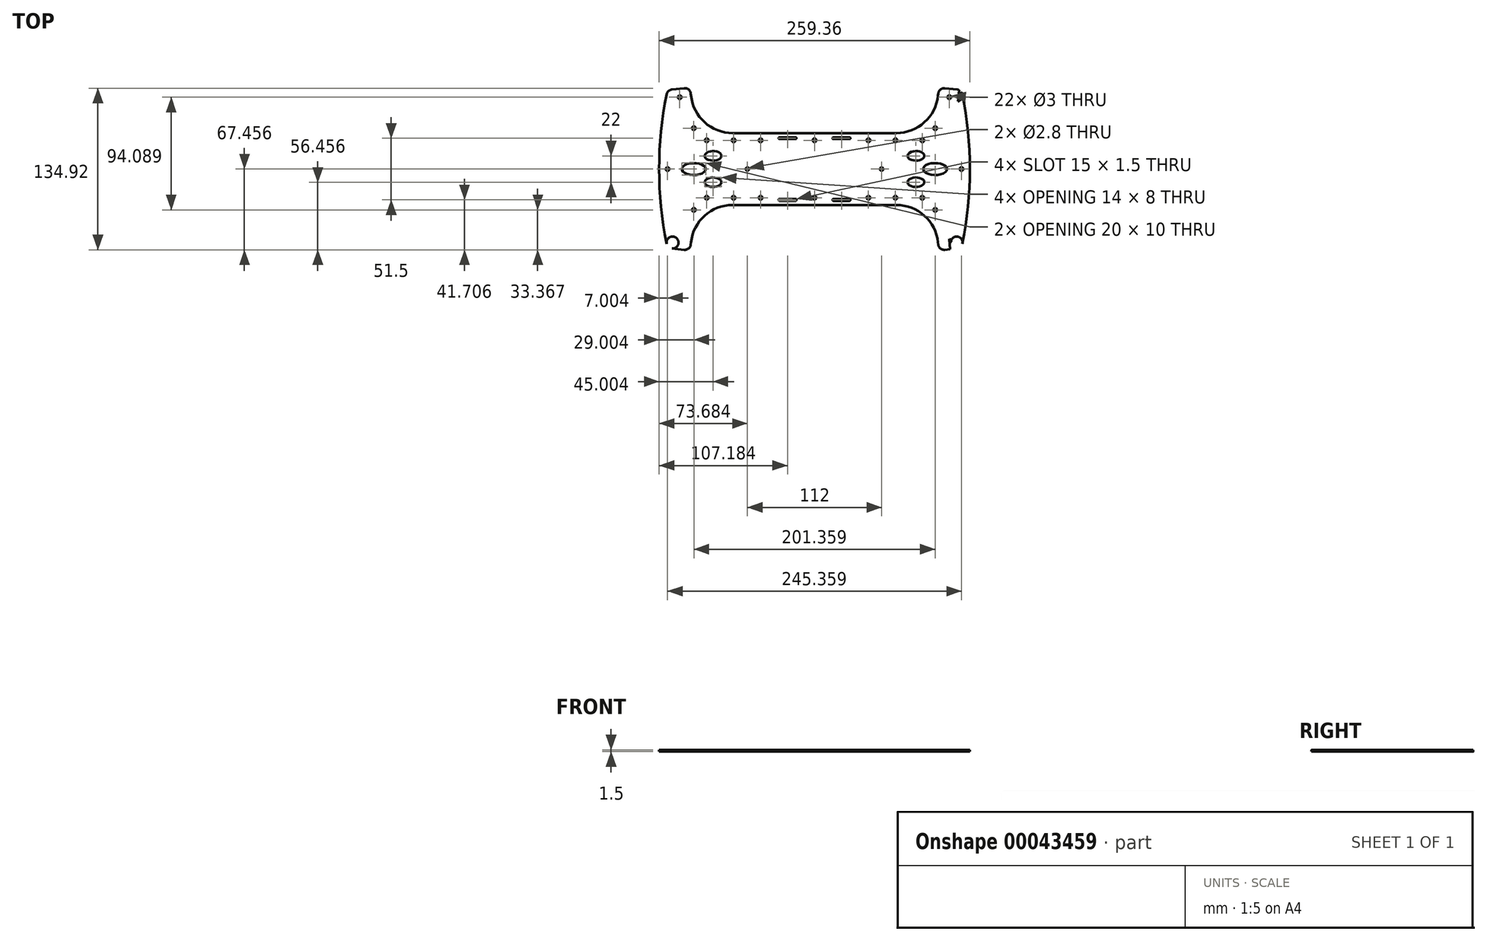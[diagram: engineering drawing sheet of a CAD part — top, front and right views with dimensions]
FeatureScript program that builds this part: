
annotation { "Feature Type Name" : "Feature", "Feature Type Description" : "" }
export const myFeature = defineFeature(function(context is Context, id is Id, definition is map)
    precondition{}
    {
        {
            var Q0;
            Q0=qCreatedBy(makeId("Top.planeOp"),FACE);
            var sketch = newSketch(context, id + "F0", { "sketchPlane" : qUnion([Q0])});
            skLineSegment(sketch, "E0", {"start": v(-133.26, 711.65) * mm, "end": v(112.1, 711.65) * mm});
            skCircle(sketch, "E1", {"center": v(-123.08, 771.65) * mm, "radius": 1.5 * mm});
            skCircle(sketch, "E2", {"center": v(-111.3, 745.73) * mm, "radius": 1.5 * mm});
            skCircle(sketch, "E3", {"center": v(90.15, 745.73) * mm, "radius": 1.5 * mm});
            skCircle(sketch, "E4", {"center": v(101.92, 771.65) * mm, "radius": 1.5 * mm});
            skLineSegment(sketch, "E5", {"start": v(-126.98, 737.05) * mm, "end": v(-131.27, 777.82) * mm});
            skLineSegment(sketch, "E6", {"start": v(-131.27, 777.82) * mm, "end": v(-116.35, 779.4) * mm});
            skLineSegment(sketch, "E7", {"start": v(-116.35, 779.4) * mm, "end": v(-112.06, 738.62) * mm});
            skLineSegment(sketch, "E8", {"start": v(-112.06, 738.62) * mm, "end": v(-126.98, 737.05) * mm});
            skLineSegment(sketch, "E9", {"start": v(-133.26, 777.61) * mm, "end": v(-119.33, 779.08) * mm});
            skLineSegment(sketch, "E10", {"start": v(-133.26, 777.61) * mm, "end": v(-133.26, 711.65) * mm});
            skLineSegment(sketch, "E11", {"start": v(95.2, 779.4) * mm, "end": v(110.11, 777.82) * mm});
            skLineSegment(sketch, "E12", {"start": v(110.11, 777.82) * mm, "end": v(105.83, 737.05) * mm});
            skLineSegment(sketch, "E13", {"start": v(105.83, 737.05) * mm, "end": v(90.91, 738.62) * mm});
            skLineSegment(sketch, "E14", {"start": v(90.91, 738.62) * mm, "end": v(95.2, 779.4) * mm});
            skLineSegment(sketch, "E15", {"start": v(98.18, 779.08) * mm, "end": v(112.1, 777.61) * mm});
            skLineSegment(sketch, "E16", {"start": v(112.1, 777.61) * mm, "end": v(112.1, 711.65) * mm});
            skLineSegment(sketch, "E17", {"start": v(-78.86, 741.65) * mm, "end": v(57.7, 741.65) * mm});
            skLineSegment(sketch, "E18", {"start": v(-113.84, 774.63) * mm, "end": v(-113.66, 772.99) * mm});
            skLineSegment(sketch, "E19", {"start": v(92.69, 774.63) * mm, "end": v(92.51, 772.99) * mm});
            skPoint(sketch, "E20.visualSharp", {"position": v(-110.37, 741.65) * mm});
            skArc(sketch, "E20.filletArc", {"start": v(-113.66, 772.99) * mm, "mid": v(-102.28, 750.64) * mm, "end": v(-78.86, 741.65) * mm});
            skPoint(sketch, "E21.visualSharp", {"position": v(89.22, 741.65) * mm});
            skArc(sketch, "E21.filletArc", {"start": v(57.7, 741.65) * mm, "mid": v(81.12, 750.64) * mm, "end": v(92.51, 772.99) * mm});
            skLineSegment(sketch, "E22.MirrorCS", {"start": v(-131.27, 645.47) * mm, "end": v(-116.35, 643.9) * mm});
            skLineSegment(sketch, "E23.MirrorCS", {"start": v(92.69, 648.66) * mm, "end": v(92.51, 650.3) * mm});
            skLineSegment(sketch, "E24.MirrorCS", {"start": v(-113.84, 648.66) * mm, "end": v(-113.66, 650.3) * mm});
            skLineSegment(sketch, "E25.MirrorCS", {"start": v(-133.26, 645.68) * mm, "end": v(-119.33, 644.21) * mm});
            skCircle(sketch, "E26.MirrorC", {"center": v(-123.08, 651.65) * mm, "radius": 1.5 * mm});
            skCircle(sketch, "E27.MirrorC", {"center": v(90.15, 677.56) * mm, "radius": 1.5 * mm});
            skCircle(sketch, "E28.MirrorC", {"center": v(-111.3, 677.56) * mm, "radius": 1.5 * mm});
            skLineSegment(sketch, "E29.MirrorCS", {"start": v(98.18, 644.21) * mm, "end": v(112.1, 645.68) * mm});
            skCircle(sketch, "E30.MirrorC", {"center": v(101.92, 651.65) * mm, "radius": 1.5 * mm});
            skPoint(sketch, "E31.MirrorP", {"position": v(-110.37, 681.65) * mm});
            skPoint(sketch, "E32.MirrorP", {"position": v(89.22, 681.65) * mm});
            skLineSegment(sketch, "E33.MirrorCS", {"start": v(110.11, 645.47) * mm, "end": v(105.83, 686.24) * mm});
            skLineSegment(sketch, "E34.MirrorCS", {"start": v(95.2, 643.9) * mm, "end": v(110.11, 645.47) * mm});
            skLineSegment(sketch, "E35.MirrorCS", {"start": v(-133.26, 645.68) * mm, "end": v(-133.26, 711.65) * mm});
            skLineSegment(sketch, "E36.MirrorCS", {"start": v(90.91, 684.68) * mm, "end": v(95.2, 643.9) * mm});
            skLineSegment(sketch, "E37.MirrorCS", {"start": v(-126.98, 686.24) * mm, "end": v(-131.27, 645.47) * mm});
            skLineSegment(sketch, "E38.MirrorCS", {"start": v(-78.86, 681.65) * mm, "end": v(57.7, 681.65) * mm});
            skLineSegment(sketch, "E39.MirrorCS", {"start": v(-116.35, 643.9) * mm, "end": v(-112.06, 684.68) * mm});
            skArc(sketch, "E40.MirrorCS", {"start": v(57.7, 681.65) * mm, "mid": v(81.12, 672.66) * mm, "end": v(92.51, 650.3) * mm});
            skLineSegment(sketch, "E41.MirrorCS", {"start": v(105.83, 686.24) * mm, "end": v(90.91, 684.68) * mm});
            skLineSegment(sketch, "E42.MirrorCS", {"start": v(-112.06, 684.68) * mm, "end": v(-126.98, 686.24) * mm});
            skArc(sketch, "E43.MirrorCS", {"start": v(-113.66, 650.3) * mm, "mid": v(-102.28, 672.66) * mm, "end": v(-78.86, 681.65) * mm});
            skLineSegment(sketch, "E44.MirrorCS", {"start": v(112.1, 645.68) * mm, "end": v(112.1, 711.65) * mm});
            skLineSegment(sketch, "E45", {"start": v(-10.58, 741.65) * mm, "end": v(-10.58, 681.65) * mm});
            skCircle(sketch, "E46", {"center": v(-66.58, 711.65) * mm, "radius": 1.4 * mm});
            skCircle(sketch, "E47", {"center": v(45.42, 711.65) * mm, "radius": 1.4 * mm});
            skArc(sketch, "E48", {"start": v(112.1, 645.68) * mm, "mid": v(119.1, 711.65) * mm, "end": v(112.1, 777.61) * mm});
            skArc(sketch, "E49", {"start": v(-133.26, 777.61) * mm, "mid": v(-140.26, 711.65) * mm, "end": v(-133.26, 645.68) * mm});
            skPoint(sketch, "E50.visualSharp", {"position": v(-133.26, 777.61) * mm});
            skPoint(sketch, "E51.visualSharp", {"position": v(-114.36, 779.6) * mm});
            skArc(sketch, "E51.filletArc", {"start": v(-113.84, 774.63) * mm, "mid": v(-115.66, 778) * mm, "end": v(-119.33, 779.08) * mm});
            skPoint(sketch, "E52.visualSharp", {"position": v(93.2, 779.6) * mm});
            skArc(sketch, "E52.filletArc", {"start": v(98.18, 779.08) * mm, "mid": v(94.51, 778) * mm, "end": v(92.69, 774.63) * mm});
            skPoint(sketch, "E53.visualSharp", {"position": v(112.1, 777.61) * mm});
            skPoint(sketch, "E54.visualSharp", {"position": v(-133.26, 645.68) * mm});
            skPoint(sketch, "E55.visualSharp", {"position": v(-114.36, 643.7) * mm});
            skArc(sketch, "E55.filletArc", {"start": v(-119.33, 644.21) * mm, "mid": v(-115.66, 645.3) * mm, "end": v(-113.84, 648.66) * mm});
            skPoint(sketch, "E56.visualSharp", {"position": v(93.2, 643.7) * mm});
            skArc(sketch, "E56.filletArc", {"start": v(92.69, 648.66) * mm, "mid": v(94.51, 645.3) * mm, "end": v(98.18, 644.21) * mm});
            skLineSegment(sketch, "E57", {"start": v(-122.32, 682.74) * mm, "end": v(-117.35, 682.21) * mm});
            skLineSegment(sketch, "E58", {"start": v(-115.57, 680.02) * mm, "end": v(-117.5, 661.62) * mm});
            skLineSegment(sketch, "E59", {"start": v(-119.7, 659.84) * mm, "end": v(-124.67, 660.36) * mm});
            skLineSegment(sketch, "E60", {"start": v(-126.45, 662.56) * mm, "end": v(-124.52, 680.96) * mm});
            skLineSegment(sketch, "E61.MirrorCS", {"start": v(101.17, 682.74) * mm, "end": v(96.2, 682.21) * mm});
            skLineSegment(sketch, "E62.MirrorCS", {"start": v(105.3, 662.56) * mm, "end": v(103.37, 680.96) * mm});
            skLineSegment(sketch, "E63.MirrorCS", {"start": v(98.55, 659.84) * mm, "end": v(103.52, 660.36) * mm});
            skLineSegment(sketch, "E64.MirrorCS", {"start": v(94.42, 680.02) * mm, "end": v(96.35, 661.62) * mm});
            skLineSegment(sketch, "E65.MirrorCS", {"start": v(101.17, 740.55) * mm, "end": v(96.2, 741.08) * mm});
            skLineSegment(sketch, "E66.MirrorCS", {"start": v(94.42, 743.27) * mm, "end": v(96.35, 761.67) * mm});
            skLineSegment(sketch, "E67.MirrorCS", {"start": v(105.3, 760.73) * mm, "end": v(103.37, 742.33) * mm});
            skLineSegment(sketch, "E68.MirrorCS", {"start": v(98.55, 763.45) * mm, "end": v(103.52, 762.93) * mm});
            skLineSegment(sketch, "E69.MirrorCS", {"start": v(-122.32, 740.55) * mm, "end": v(-117.35, 741.08) * mm});
            skLineSegment(sketch, "E70.MirrorCS", {"start": v(-126.45, 760.73) * mm, "end": v(-124.52, 742.33) * mm});
            skLineSegment(sketch, "E71.MirrorCS", {"start": v(-115.57, 743.27) * mm, "end": v(-117.5, 761.67) * mm});
            skLineSegment(sketch, "E72.MirrorCS", {"start": v(-119.7, 763.45) * mm, "end": v(-124.67, 762.93) * mm});
            skCircle(sketch, "E73", {"center": v(-10.58, 735.65) * mm, "radius": 1.5 * mm});
            skCircle(sketch, "E74", {"center": v(-55.58, 735.65) * mm, "radius": 1.5 * mm});
            skCircle(sketch, "E75", {"center": v(-100.58, 735.65) * mm, "radius": 1.5 * mm});
            skCircle(sketch, "E76.MirrorC", {"center": v(34.42, 735.65) * mm, "radius": 1.5 * mm});
            skCircle(sketch, "E77.MirrorC", {"center": v(79.42, 735.65) * mm, "radius": 1.5 * mm});
            skCircle(sketch, "E78.MirrorC", {"center": v(-55.58, 687.65) * mm, "radius": 1.5 * mm});
            skCircle(sketch, "E79.MirrorC", {"center": v(-10.58, 687.65) * mm, "radius": 1.5 * mm});
            skCircle(sketch, "E80.MirrorC", {"center": v(34.42, 687.65) * mm, "radius": 1.5 * mm});
            skCircle(sketch, "E81.MirrorC", {"center": v(79.42, 687.65) * mm, "radius": 1.5 * mm});
            skCircle(sketch, "E82.MirrorC", {"center": v(-100.58, 687.65) * mm, "radius": 1.5 * mm});
            skCircle(sketch, "E83", {"center": v(-133.26, 711.65) * mm, "radius": 1.5 * mm});
            skCircle(sketch, "E84.MirrorC", {"center": v(112.1, 711.65) * mm, "radius": 1.5 * mm});
            skLineSegment(sketch, "E85", {"start": v(-119.52, 737.83) * mm, "end": v(-134.26, 878.06) * mm});
            skLineSegment(sketch, "E86", {"start": v(98.37, 737.83) * mm, "end": v(113.1, 878.06) * mm});
            skLineSegment(sketch, "E87", {"start": v(98.37, 685.46) * mm, "end": v(113.1, 545.23) * mm});
            skLineSegment(sketch, "E88.bottom", {"start": v(-39.83, 738.15) * mm, "end": v(-26.33, 738.15) * mm});
            skLineSegment(sketch, "E88.top", {"start": v(-39.83, 736.65) * mm, "end": v(-26.33, 736.65) * mm});
            skLineSegment(sketch, "E88.left", {"start": v(-40.58, 737.4) * mm, "end": v(-40.58, 737.4) * mm});
            skLineSegment(sketch, "E88.right", {"start": v(-25.58, 737.4) * mm, "end": v(-25.58, 737.4) * mm});
            skLineSegment(sketch, "E89.bottom", {"start": v(5.17, 738.15) * mm, "end": v(18.67, 738.15) * mm});
            skLineSegment(sketch, "E89.top", {"start": v(5.17, 736.65) * mm, "end": v(18.67, 736.65) * mm});
            skLineSegment(sketch, "E89.left", {"start": v(4.42, 737.4) * mm, "end": v(4.42, 737.4) * mm});
            skLineSegment(sketch, "E89.right", {"start": v(19.42, 737.4) * mm, "end": v(19.42, 737.4) * mm});
            skPoint(sketch, "E90.visualSharp", {"position": v(-40.58, 738.15) * mm});
            skArc(sketch, "E90.filletArc", {"start": v(-39.83, 738.15) * mm, "mid": v(-40.36, 737.93) * mm, "end": v(-40.58, 737.4) * mm});
            skPoint(sketch, "E91.visualSharp", {"position": v(-40.58, 736.65) * mm});
            skArc(sketch, "E91.filletArc", {"start": v(-40.58, 737.4) * mm, "mid": v(-40.36, 736.87) * mm, "end": v(-39.83, 736.65) * mm});
            skPoint(sketch, "E92.visualSharp", {"position": v(-25.58, 738.15) * mm});
            skArc(sketch, "E92.filletArc", {"start": v(-25.58, 737.4) * mm, "mid": v(-25.8, 737.93) * mm, "end": v(-26.33, 738.15) * mm});
            skPoint(sketch, "E93.visualSharp", {"position": v(-25.58, 736.65) * mm});
            skArc(sketch, "E93.filletArc", {"start": v(-26.33, 736.65) * mm, "mid": v(-25.8, 736.87) * mm, "end": v(-25.58, 737.4) * mm});
            skPoint(sketch, "E94.visualSharp", {"position": v(4.42, 738.15) * mm});
            skArc(sketch, "E94.filletArc", {"start": v(5.17, 738.15) * mm, "mid": v(4.64, 737.93) * mm, "end": v(4.42, 737.4) * mm});
            skPoint(sketch, "E95.visualSharp", {"position": v(4.42, 736.65) * mm});
            skArc(sketch, "E95.filletArc", {"start": v(4.42, 737.4) * mm, "mid": v(4.64, 736.87) * mm, "end": v(5.17, 736.65) * mm});
            skPoint(sketch, "E96.visualSharp", {"position": v(19.42, 738.15) * mm});
            skArc(sketch, "E96.filletArc", {"start": v(19.42, 737.4) * mm, "mid": v(19.2, 737.93) * mm, "end": v(18.67, 738.15) * mm});
            skPoint(sketch, "E97.visualSharp", {"position": v(19.42, 736.65) * mm});
            skArc(sketch, "E97.filletArc", {"start": v(18.67, 736.65) * mm, "mid": v(19.2, 736.87) * mm, "end": v(19.42, 737.4) * mm});
            skArc(sketch, "E98.MirrorCS", {"start": v(5.17, 685.15) * mm, "mid": v(4.64, 685.37) * mm, "end": v(4.42, 685.9) * mm});
            skArc(sketch, "E99.MirrorCS", {"start": v(18.67, 686.65) * mm, "mid": v(19.2, 686.43) * mm, "end": v(19.42, 685.9) * mm});
            skArc(sketch, "E100.MirrorCS", {"start": v(19.42, 685.9) * mm, "mid": v(19.2, 685.37) * mm, "end": v(18.67, 685.15) * mm});
            skArc(sketch, "E101.MirrorCS", {"start": v(4.42, 685.9) * mm, "mid": v(4.64, 686.43) * mm, "end": v(5.17, 686.65) * mm});
            skLineSegment(sketch, "E102.MirrorCS", {"start": v(19.42, 685.9) * mm, "end": v(19.42, 685.9) * mm});
            skLineSegment(sketch, "E103.MirrorCS", {"start": v(4.42, 685.9) * mm, "end": v(4.42, 685.9) * mm});
            skPoint(sketch, "E104.MirrorP", {"position": v(19.42, 686.65) * mm});
            skLineSegment(sketch, "E105.MirrorCS", {"start": v(5.17, 686.65) * mm, "end": v(18.67, 686.65) * mm});
            skLineSegment(sketch, "E106.MirrorCS", {"start": v(5.17, 685.15) * mm, "end": v(18.67, 685.15) * mm});
            skPoint(sketch, "E107.MirrorP", {"position": v(19.42, 685.15) * mm});
            skPoint(sketch, "E108.MirrorP", {"position": v(4.42, 686.65) * mm});
            skPoint(sketch, "E109.MirrorP", {"position": v(4.42, 685.15) * mm});
            skArc(sketch, "E110.MirrorCS", {"start": v(-25.58, 685.9) * mm, "mid": v(-25.8, 685.37) * mm, "end": v(-26.33, 685.15) * mm});
            skArc(sketch, "E111.MirrorCS", {"start": v(-39.83, 685.15) * mm, "mid": v(-40.36, 685.37) * mm, "end": v(-40.58, 685.9) * mm});
            skArc(sketch, "E112.MirrorCS", {"start": v(-40.58, 685.9) * mm, "mid": v(-40.36, 686.43) * mm, "end": v(-39.83, 686.65) * mm});
            skArc(sketch, "E113.MirrorCS", {"start": v(-26.33, 686.65) * mm, "mid": v(-25.8, 686.43) * mm, "end": v(-25.58, 685.9) * mm});
            skLineSegment(sketch, "E114.MirrorCS", {"start": v(-25.58, 685.9) * mm, "end": v(-25.58, 685.9) * mm});
            skLineSegment(sketch, "E115.MirrorCS", {"start": v(-40.58, 685.9) * mm, "end": v(-40.58, 685.9) * mm});
            skPoint(sketch, "E116.MirrorP", {"position": v(-40.58, 685.15) * mm});
            skLineSegment(sketch, "E117.MirrorCS", {"start": v(-39.83, 685.15) * mm, "end": v(-26.33, 685.15) * mm});
            skPoint(sketch, "E118.MirrorP", {"position": v(-25.58, 685.15) * mm});
            skLineSegment(sketch, "E119.MirrorCS", {"start": v(-39.83, 686.65) * mm, "end": v(-26.33, 686.65) * mm});
            skPoint(sketch, "E120.MirrorP", {"position": v(-40.58, 686.65) * mm});
            skPoint(sketch, "E121.MirrorP", {"position": v(-25.58, 686.65) * mm});
            skEllipse(sketch, "E122", {"center": v(-95.26, 722.65) * mm, "majorRadius": 4 * mm, "minorRadius": 7 * mm, "majorAxis": v(0, -1)});
            skEllipse(sketch, "E123", {"center": v(-95.26, 700.65) * mm, "majorRadius": 4 * mm, "minorRadius": 7 * mm, "majorAxis": v(0, -1)});
            skEllipse(sketch, "E124", {"center": v(-111.26, 711.65) * mm, "majorRadius": 5 * mm, "minorRadius": 10 * mm, "majorAxis": v(0, -1)});
            skPoint(sketch, "E125", {"position": v(-102.26, 722.65) * mm});
            skPoint(sketch, "E125.positionSnap0", {"position": v(-102.26, 722.65) * mm});
            skPoint(sketch, "E126", {"position": v(-102.26, 700.65) * mm});
            skPoint(sketch, "E127", {"position": v(-121.26, 711.65) * mm});
            skPoint(sketch, "E128.MirrorP", {"position": v(81.1, 722.65) * mm});
            skEllipse(sketch, "E129.MirrorC", {"center": v(90.1, 711.65) * mm, "majorRadius": 5 * mm, "minorRadius": 10 * mm, "majorAxis": v(0, -1)});
            skEllipse(sketch, "E130.MirrorC", {"center": v(74.1, 722.65) * mm, "majorRadius": 4 * mm, "minorRadius": 7 * mm, "majorAxis": v(0, -1)});
            skPoint(sketch, "E131.MirrorP", {"position": v(81.1, 700.65) * mm});
            skEllipse(sketch, "E132.MirrorC", {"center": v(74.1, 700.65) * mm, "majorRadius": 4 * mm, "minorRadius": 7 * mm, "majorAxis": v(0, -1)});
            skPoint(sketch, "E133.visualSharp", {"position": v(-126.66, 762.72) * mm});
            skArc(sketch, "E133.filletArc", {"start": v(-124.67, 762.93) * mm, "mid": v(-126.02, 762.2) * mm, "end": v(-126.45, 760.73) * mm});
            skPoint(sketch, "E134.visualSharp", {"position": v(-117.71, 763.66) * mm});
            skArc(sketch, "E134.filletArc", {"start": v(-117.5, 761.67) * mm, "mid": v(-118.23, 763.02) * mm, "end": v(-119.7, 763.45) * mm});
            skPoint(sketch, "E135.visualSharp", {"position": v(-124.31, 740.35) * mm});
            skArc(sketch, "E135.filletArc", {"start": v(-124.52, 742.33) * mm, "mid": v(-123.79, 740.99) * mm, "end": v(-122.32, 740.55) * mm});
            skPoint(sketch, "E136.visualSharp", {"position": v(-115.36, 741.29) * mm});
            skArc(sketch, "E136.filletArc", {"start": v(-117.35, 741.08) * mm, "mid": v(-116, 741.8) * mm, "end": v(-115.57, 743.27) * mm});
            skPoint(sketch, "E137.visualSharp", {"position": v(-124.31, 682.95) * mm});
            skArc(sketch, "E137.filletArc", {"start": v(-122.32, 682.74) * mm, "mid": v(-123.79, 682.3) * mm, "end": v(-124.52, 680.96) * mm});
            skPoint(sketch, "E138.visualSharp", {"position": v(-126.66, 660.57) * mm});
            skArc(sketch, "E138.filletArc", {"start": v(-126.45, 662.56) * mm, "mid": v(-126.02, 661.1) * mm, "end": v(-124.67, 660.36) * mm});
            skPoint(sketch, "E139.visualSharp", {"position": v(-115.36, 682) * mm});
            skArc(sketch, "E139.filletArc", {"start": v(-115.57, 680.02) * mm, "mid": v(-116, 681.48) * mm, "end": v(-117.35, 682.21) * mm});
            skPoint(sketch, "E140.visualSharp", {"position": v(-117.71, 659.63) * mm});
            skArc(sketch, "E140.filletArc", {"start": v(-119.7, 659.84) * mm, "mid": v(-118.23, 660.27) * mm, "end": v(-117.5, 661.62) * mm});
            skPoint(sketch, "E141.visualSharp", {"position": v(94.2, 682) * mm});
            skArc(sketch, "E141.filletArc", {"start": v(96.2, 682.21) * mm, "mid": v(94.85, 681.48) * mm, "end": v(94.42, 680.02) * mm});
            skPoint(sketch, "E142.visualSharp", {"position": v(103.16, 682.95) * mm});
            skArc(sketch, "E142.filletArc", {"start": v(103.37, 680.96) * mm, "mid": v(102.64, 682.3) * mm, "end": v(101.17, 682.74) * mm});
            skPoint(sketch, "E143.visualSharp", {"position": v(105.51, 660.57) * mm});
            skArc(sketch, "E143.filletArc", {"start": v(103.52, 660.36) * mm, "mid": v(104.87, 661.1) * mm, "end": v(105.3, 662.56) * mm});
            skPoint(sketch, "E144.visualSharp", {"position": v(96.56, 659.63) * mm});
            skArc(sketch, "E144.filletArc", {"start": v(96.35, 661.62) * mm, "mid": v(97.08, 660.27) * mm, "end": v(98.55, 659.84) * mm});
            skPoint(sketch, "E145.visualSharp", {"position": v(105.51, 762.72) * mm});
            skArc(sketch, "E145.filletArc", {"start": v(105.3, 760.73) * mm, "mid": v(104.87, 762.2) * mm, "end": v(103.52, 762.93) * mm});
            skPoint(sketch, "E146.visualSharp", {"position": v(103.16, 740.35) * mm});
            skArc(sketch, "E146.filletArc", {"start": v(101.17, 740.55) * mm, "mid": v(102.64, 740.99) * mm, "end": v(103.37, 742.33) * mm});
            skPoint(sketch, "E147.visualSharp", {"position": v(96.56, 763.66) * mm});
            skArc(sketch, "E147.filletArc", {"start": v(98.55, 763.45) * mm, "mid": v(97.08, 763.02) * mm, "end": v(96.35, 761.67) * mm});
            skPoint(sketch, "E148.visualSharp", {"position": v(94.2, 741.29) * mm});
            skArc(sketch, "E148.filletArc", {"start": v(94.42, 743.27) * mm, "mid": v(94.85, 741.8) * mm, "end": v(96.2, 741.08) * mm});
            skCircle(sketch, "E149", {"center": v(-78.08, 735.65) * mm, "radius": 1.5 * mm});
            skCircle(sketch, "E150.MirrorC", {"center": v(56.92, 735.65) * mm, "radius": 1.5 * mm});
            skCircle(sketch, "E151.MirrorC", {"center": v(-78.08, 687.65) * mm, "radius": 1.5 * mm});
            skCircle(sketch, "E152.MirrorC", {"center": v(56.92, 687.65) * mm, "radius": 1.5 * mm});
            skCircle(sketch, "E153", {"center": v(107.95, 773.02) * mm, "radius": 5 * mm});
            skCircle(sketch, "E154", {"center": v(107.95, 650.27) * mm, "radius": 5 * mm});
            skCircle(sketch, "E155", {"center": v(-129.1, 650.27) * mm, "radius": 5 * mm});
            skCircle(sketch, "E156", {"center": v(-129.1, 773.02) * mm, "radius": 5 * mm});
            skSolve(sketch);
        }
        {
            var Q0;
            {var subQ9=sQuery(id+"F0.wireOp",EDGE,"E24.MirrorCS");Q0=makeQuery(id+"F0.imprint","IMPRINT",FACE,{"disambiguationData":[TD([[makeQuery(id+"F0.imprint","IMPRINT",EDGE,{"derivedFrom":subQ9}),1.0]])]});}
            var Q1;
            {var subQ12=sQuery(id+"F0.wireOp",EDGE,"E2");Q1=makeQuery(id+"F0.imprint","IMPRINT",FACE,{"disambiguationData":[TD([[makeQuery(id+"F0.imprint","IMPRINT",EDGE,{"derivedFrom":subQ12}),-1.0]])]});}
            var Q2;
            {var subQ19=sQuery(id+"F0.wireOp",EDGE,"E3");Q2=makeQuery(id+"F0.imprint","IMPRINT",FACE,{"disambiguationData":[TD([[makeQuery(id+"F0.imprint","IMPRINT",EDGE,{"derivedFrom":subQ19}),-1.0]])]});}
            var Q3;
            {var subQ27=sQuery(id+"F0.wireOp",EDGE,"E23.MirrorCS");Q3=makeQuery(id+"F0.imprint","IMPRINT",FACE,{"disambiguationData":[TD([[makeQuery(id+"F0.imprint","IMPRINT",EDGE,{"derivedFrom":subQ27}),-1.0]])]});}
            var Q4;
            Q4=makeQuery(id+"F0.imprint","IMPRINT",FACE,{"disambiguationData":[TD([[makeQuery(id+"F0.imprint","IMPRINT",EDGE,{"derivedFrom":sQuery(id+"F0.wireOp",EDGE,"E71.MirrorCS")}),-1.0]])]});
            var Q5;
            Q5=makeQuery(id+"F0.imprint","IMPRINT",FACE,{"disambiguationData":[TD([[makeQuery(id+"F0.imprint","IMPRINT",EDGE,{"derivedFrom":sQuery(id+"F0.wireOp",EDGE,"E71.MirrorCS")}),1.0]])]});
            var Q6;
            Q6=makeQuery(id+"F0.imprint","IMPRINT",FACE,{"disambiguationData":[TD([[makeQuery(id+"F0.imprint","IMPRINT",EDGE,{"derivedFrom":sQuery(id+"F0.wireOp",EDGE,"E70.MirrorCS")}),1.0]])]});
            var Q7;
            Q7=makeQuery(id+"F0.imprint","IMPRINT",FACE,{"disambiguationData":[TD([[makeQuery(id+"F0.imprint","IMPRINT",EDGE,{"derivedFrom":sQuery(id+"F0.wireOp",EDGE,"E70.MirrorCS")}),-1.0]])]});
            var Q8;
            {var subQ9=sQuery(id+"F0.wireOp",EDGE,"E42.MirrorCS");Q8=makeQuery(id+"F0.imprint","IMPRINT",FACE,{"disambiguationData":[TD([[makeQuery(id+"F0.imprint","IMPRINT",EDGE,{"derivedFrom":subQ9}),1.0]])]});}
            var Q9;
            Q9=makeQuery(id+"F0.imprint","IMPRINT",FACE,{"disambiguationData":[TD([[makeQuery(id+"F0.imprint","IMPRINT",EDGE,{"derivedFrom":sQuery(id+"F0.wireOp",EDGE,"E57")}),-1.0]])]});
            var Q10;
            Q10=makeQuery(id+"F0.imprint","IMPRINT",FACE,{"disambiguationData":[TD([[makeQuery(id+"F0.imprint","IMPRINT",EDGE,{"derivedFrom":sQuery(id+"F0.wireOp",EDGE,"E64.MirrorCS")}),-1.0]])]});
            var Q11;
            Q11=makeQuery(id+"F0.imprint","IMPRINT",FACE,{"disambiguationData":[TD([[makeQuery(id+"F0.imprint","IMPRINT",EDGE,{"derivedFrom":sQuery(id+"F0.wireOp",EDGE,"E64.MirrorCS")}),1.0]])]});
            var Q12;
            Q12=makeQuery(id+"F0.imprint","IMPRINT",FACE,{"disambiguationData":[TD([[makeQuery(id+"F0.imprint","IMPRINT",EDGE,{"derivedFrom":sQuery(id+"F0.wireOp",EDGE,"E62.MirrorCS")}),1.0]])]});
            var Q13;
            Q13=makeQuery(id+"F0.imprint","IMPRINT",FACE,{"disambiguationData":[TD([[makeQuery(id+"F0.imprint","IMPRINT",EDGE,{"derivedFrom":sQuery(id+"F0.wireOp",EDGE,"E62.MirrorCS")}),-1.0]])]});
            var Q14;
            Q14=makeQuery(id+"F0.imprint","IMPRINT",FACE,{"disambiguationData":[TD([[makeQuery(id+"F0.imprint","IMPRINT",EDGE,{"derivedFrom":sQuery(id+"F0.wireOp",EDGE,"E66.MirrorCS")}),1.0]])]});
            var Q15;
            Q15=makeQuery(id+"F0.imprint","IMPRINT",FACE,{"disambiguationData":[TD([[makeQuery(id+"F0.imprint","IMPRINT",EDGE,{"derivedFrom":sQuery(id+"F0.wireOp",EDGE,"E66.MirrorCS")}),-1.0]])]});
            var Q16;
            Q16=makeQuery(id+"F0.imprint","IMPRINT",FACE,{"disambiguationData":[TD([[makeQuery(id+"F0.imprint","IMPRINT",EDGE,{"derivedFrom":sQuery(id+"F0.wireOp",EDGE,"E67.MirrorCS")}),-1.0]])]});
            var Q17;
            Q17=makeQuery(id+"F0.imprint","IMPRINT",FACE,{"disambiguationData":[TD([[makeQuery(id+"F0.imprint","IMPRINT",EDGE,{"derivedFrom":sQuery(id+"F0.wireOp",EDGE,"E67.MirrorCS")}),1.0]])]});
            var Q18;
            {var subQ0=sQuery(id+"F0.wireOp",EDGE,"E153");var subQ1=sQuery(id+"F0.wireOp",EDGE,"E16");var subQ2=makeQuery(id+"F0.imprint","INTERSECT",VERTEX,{"disambiguationData":[OD(0.0)],"derivedFrom":[subQ1,subQ0]});Q18=makeQuery(id+"F0.imprint","IMPRINT",FACE,{"disambiguationData":[TD([[makeQuery(id+"F0.imprint","IMPRINT",EDGE,{"disambiguationData":[TD([[subQ2,-1.0]])],"derivedFrom":subQ1}),1.0]])]});}
            var Q19;
            {var subQ0=sQuery(id+"F0.wireOp",EDGE,"E153");var subQ1=sQuery(id+"F0.wireOp",EDGE,"E12");var subQ2=makeQuery(id+"F0.imprint","INTERSECT",VERTEX,{"disambiguationData":[OD(0.0)],"derivedFrom":[subQ1,subQ0]});Q19=makeQuery(id+"F0.imprint","IMPRINT",FACE,{"disambiguationData":[TD([[makeQuery(id+"F0.imprint","IMPRINT",EDGE,{"disambiguationData":[TD([[subQ2,-1.0]])],"derivedFrom":subQ1}),1.0]])]});}
            var Q20;
            {var subQ0=sQuery(id+"F0.wireOp",EDGE,"E153");var subQ2=sQuery(id+"F0.wireOp",EDGE,"E4");var subQ3=makeQuery(id+"F0.imprint","INTERSECT",VERTEX,{"disambiguationData":[OD(0.0)],"derivedFrom":[subQ2,subQ0]});Q20=makeQuery(id+"F0.imprint","IMPRINT",FACE,{"disambiguationData":[TD([[makeQuery(id+"F0.imprint","IMPRINT",EDGE,{"disambiguationData":[TD([[subQ3,1.0]])],"derivedFrom":subQ2}),-1.0]])]});}
            var Q21;
            {var subQ0=sQuery(id+"F0.wireOp",EDGE,"E86");var subQ1=sQuery(id+"F0.wireOp",EDGE,"E4");var subQ2=makeQuery(id+"F0.imprint","INTERSECT",VERTEX,{"disambiguationData":[OD(0.0)],"derivedFrom":[subQ1,subQ0]});Q21=makeQuery(id+"F0.imprint","IMPRINT",FACE,{"disambiguationData":[TD([[makeQuery(id+"F0.imprint","IMPRINT",EDGE,{"disambiguationData":[TD([[subQ2,1.0]])],"derivedFrom":subQ1}),-1.0]])]});}
            var Q22;
            {var subQ1=sQuery(id+"F0.wireOp",EDGE,"E16");var subQ5=sQuery(id+"F0.wireOp",EDGE,"E153");var subQ6=makeQuery(id+"F0.imprint","INTERSECT",VERTEX,{"disambiguationData":[OD(1.0)],"derivedFrom":[subQ1,subQ5]});Q22=makeQuery(id+"F0.imprint","IMPRINT",FACE,{"disambiguationData":[TD([[makeQuery(id+"F0.imprint","IMPRINT",EDGE,{"disambiguationData":[TD([[subQ6,-1.0]])],"derivedFrom":subQ1}),1.0]])]});}
            var Q23;
            {var subQ0=sQuery(id+"F0.wireOp",EDGE,"E154");var subQ1=sQuery(id+"F0.wireOp",EDGE,"E44.MirrorCS");var subQ2=makeQuery(id+"F0.imprint","INTERSECT",VERTEX,{"disambiguationData":[OD(0.0)],"derivedFrom":[subQ1,subQ0]});Q23=makeQuery(id+"F0.imprint","IMPRINT",FACE,{"disambiguationData":[TD([[makeQuery(id+"F0.imprint","IMPRINT",EDGE,{"disambiguationData":[TD([[subQ2,-1.0]])],"derivedFrom":subQ1}),-1.0]])]});}
            var Q24;
            {var subQ0=sQuery(id+"F0.wireOp",EDGE,"E154");var subQ1=sQuery(id+"F0.wireOp",EDGE,"E33.MirrorCS");var subQ2=makeQuery(id+"F0.imprint","INTERSECT",VERTEX,{"disambiguationData":[OD(0.0)],"derivedFrom":[subQ1,subQ0]});Q24=makeQuery(id+"F0.imprint","IMPRINT",FACE,{"disambiguationData":[TD([[makeQuery(id+"F0.imprint","IMPRINT",EDGE,{"disambiguationData":[TD([[subQ2,-1.0]])],"derivedFrom":subQ1}),-1.0]])]});}
            var Q25;
            {var subQ0=sQuery(id+"F0.wireOp",EDGE,"E154");var subQ1=sQuery(id+"F0.wireOp",EDGE,"E30.MirrorC");var subQ6=makeQuery(id+"F0.imprint","INTERSECT",VERTEX,{"disambiguationData":[OD(0.0)],"derivedFrom":[subQ1,subQ0]});Q25=makeQuery(id+"F0.imprint","IMPRINT",FACE,{"disambiguationData":[TD([[makeQuery(id+"F0.imprint","IMPRINT",EDGE,{"disambiguationData":[TD([[subQ6,1.0]])],"derivedFrom":subQ1}),1.0]])]});}
            var Q26;
            {var subQ0=sQuery(id+"F0.wireOp",EDGE,"E87");var subQ1=sQuery(id+"F0.wireOp",EDGE,"E30.MirrorC");var subQ2=makeQuery(id+"F0.imprint","INTERSECT",VERTEX,{"disambiguationData":[OD(0.0)],"derivedFrom":[subQ1,subQ0]});Q26=makeQuery(id+"F0.imprint","IMPRINT",FACE,{"disambiguationData":[TD([[makeQuery(id+"F0.imprint","IMPRINT",EDGE,{"disambiguationData":[TD([[subQ2,1.0]])],"derivedFrom":subQ1}),1.0]])]});}
            var Q27;
            {var subQ0=sQuery(id+"F0.wireOp",EDGE,"E155");var subQ1=sQuery(id+"F0.wireOp",EDGE,"E26.MirrorC");var subQ2=makeQuery(id+"F0.imprint","INTERSECT",VERTEX,{"disambiguationData":[OD(0.0)],"derivedFrom":[subQ1,subQ0]});Q27=makeQuery(id+"F0.imprint","IMPRINT",FACE,{"disambiguationData":[TD([[makeQuery(id+"F0.imprint","IMPRINT",EDGE,{"disambiguationData":[TD([[subQ2,1.0]])],"derivedFrom":subQ1}),1.0]])]});}
            var Q28;
            {var subQ0=sQuery(id+"F0.wireOp",EDGE,"E155");var subQ1=sQuery(id+"F0.wireOp",EDGE,"E35.MirrorCS");var subQ2=makeQuery(id+"F0.imprint","INTERSECT",VERTEX,{"disambiguationData":[OD(0.0)],"derivedFrom":[subQ1,subQ0]});Q28=makeQuery(id+"F0.imprint","IMPRINT",FACE,{"disambiguationData":[TD([[makeQuery(id+"F0.imprint","IMPRINT",EDGE,{"disambiguationData":[TD([[subQ2,-1.0]])],"derivedFrom":subQ1}),-1.0]])]});}
            var Q29;
            {var subQ0=sQuery(id+"F0.wireOp",EDGE,"E155");var subQ1=sQuery(id+"F0.wireOp",EDGE,"E35.MirrorCS");var subQ2=makeQuery(id+"F0.imprint","INTERSECT",VERTEX,{"disambiguationData":[OD(0.0)],"derivedFrom":[subQ1,subQ0]});Q29=makeQuery(id+"F0.imprint","IMPRINT",FACE,{"disambiguationData":[TD([[makeQuery(id+"F0.imprint","IMPRINT",EDGE,{"disambiguationData":[TD([[subQ2,-1.0]])],"derivedFrom":subQ1}),1.0]])]});}
            var Q30;
            {var subQ1=sQuery(id+"F0.wireOp",EDGE,"E10");var subQ5=sQuery(id+"F0.wireOp",EDGE,"E156");var subQ8=makeQuery(id+"F0.imprint","INTERSECT",VERTEX,{"disambiguationData":[OD(1.0)],"derivedFrom":[subQ1,subQ5]});Q30=makeQuery(id+"F0.imprint","IMPRINT",FACE,{"disambiguationData":[TD([[makeQuery(id+"F0.imprint","IMPRINT",EDGE,{"disambiguationData":[TD([[subQ8,-1.0]])],"derivedFrom":subQ1}),-1.0]])]});}
            var Q31;
            {var subQ0=sQuery(id+"F0.wireOp",EDGE,"E156");var subQ1=sQuery(id+"F0.wireOp",EDGE,"E10");var subQ2=makeQuery(id+"F0.imprint","INTERSECT",VERTEX,{"disambiguationData":[OD(0.0)],"derivedFrom":[subQ1,subQ0]});Q31=makeQuery(id+"F0.imprint","IMPRINT",FACE,{"disambiguationData":[TD([[makeQuery(id+"F0.imprint","IMPRINT",EDGE,{"disambiguationData":[TD([[subQ2,-1.0]])],"derivedFrom":subQ1}),-1.0]])]});}
            var Q32;
            {var subQ0=sQuery(id+"F0.wireOp",EDGE,"E156");var subQ1=sQuery(id+"F0.wireOp",EDGE,"E5");var subQ2=makeQuery(id+"F0.imprint","INTERSECT",VERTEX,{"disambiguationData":[OD(0.0)],"derivedFrom":[subQ1,subQ0]});Q32=makeQuery(id+"F0.imprint","IMPRINT",FACE,{"disambiguationData":[TD([[makeQuery(id+"F0.imprint","IMPRINT",EDGE,{"disambiguationData":[TD([[subQ2,-1.0]])],"derivedFrom":subQ1}),1.0]])]});}
            var Q33;
            {var subQ0=sQuery(id+"F0.wireOp",EDGE,"E156");var subQ1=sQuery(id+"F0.wireOp",EDGE,"E1");var subQ5=makeQuery(id+"F0.imprint","INTERSECT",VERTEX,{"disambiguationData":[OD(0.0)],"derivedFrom":[subQ1,subQ0]});Q33=makeQuery(id+"F0.imprint","IMPRINT",FACE,{"disambiguationData":[TD([[makeQuery(id+"F0.imprint","IMPRINT",EDGE,{"disambiguationData":[TD([[subQ5,-1.0]])],"derivedFrom":subQ1}),-1.0]])]});}
            var Q34;
            {var subQ0=sQuery(id+"F0.wireOp",EDGE,"E156");var subQ1=sQuery(id+"F0.wireOp",EDGE,"E1");var subQ2=makeQuery(id+"F0.imprint","INTERSECT",VERTEX,{"disambiguationData":[OD(0.0)],"derivedFrom":[subQ1,subQ0]});Q34=makeQuery(id+"F0.imprint","IMPRINT",FACE,{"disambiguationData":[TD([[makeQuery(id+"F0.imprint","IMPRINT",EDGE,{"disambiguationData":[TD([[subQ2,1.0]])],"derivedFrom":subQ1}),-1.0]])]});}
            extrude(context, id + "F1", {"entities" : qUnion([Q0, Q1, Q2, Q3, Q4, Q5, Q6, Q7, Q8, Q9, Q10, Q11, Q12, Q13, Q14, Q15, Q16, Q17, Q18, Q19, Q20, Q21, Q22, Q23, Q24, Q25, Q26, Q27, Q28, Q29, Q30, Q31, Q32, Q33, Q34]), "depth" : 1.5 * mm});
        }
    });
